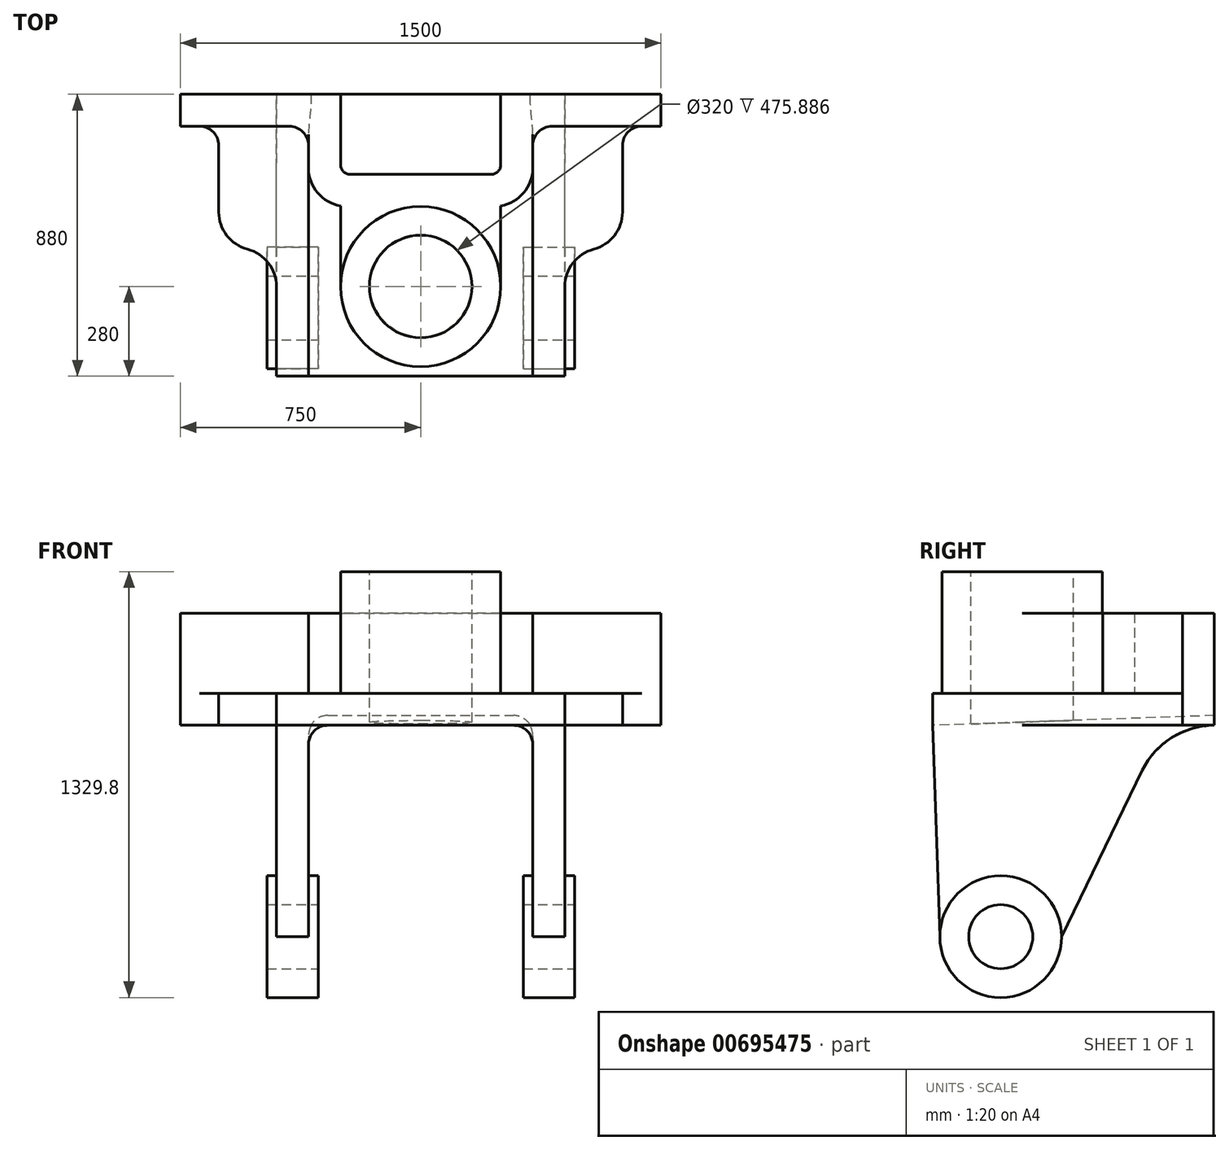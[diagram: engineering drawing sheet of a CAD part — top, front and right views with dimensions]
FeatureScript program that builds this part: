
annotation { "Feature Type Name" : "Feature", "Feature Type Description" : "" }
export const myFeature = defineFeature(function(context is Context, id is Id, definition is map)
    precondition{}
    {
        {
            var Q0;
            Q0=qCreatedBy(makeId("Top.planeOp"),FACE);
            var sketch = newSketch(context, id + "F0", { "sketchPlane" : qUnion([Q0])});
            skLineSegment(sketch, "E0.bottom", {"start": v(-750, 440) * mm, "end": v(750, 440) * mm});
            skLineSegment(sketch, "E0.top", {"start": v(-450, -440) * mm, "end": v(450, -440) * mm});
            skLineSegment(sketch, "E0.right", {"start": v(750, 440) * mm, "end": v(750, 340) * mm});
            skPoint(sketch, "E0.middle", {"position": v(0, 0) * mm});
            skArc(sketch, "E1", {"start": v(690, 340) * mm, "mid": v(647.57, 322.43) * mm, "end": v(630, 280) * mm});
            skLineSegment(sketch, "E2", {"start": v(450, -440) * mm, "end": v(450, -160) * mm});
            skArc(sketch, "E3", {"start": v(540, -43.81) * mm, "mid": v(475.13, -86.52) * mm, "end": v(450, -160) * mm});
            skArc(sketch, "E4.trimOffspring", {"start": v(540, -43.81) * mm, "mid": v(604.87, -1.1) * mm, "end": v(630, 72.38) * mm});
            skLineSegment(sketch, "E5.trimOffspring", {"start": v(690, 340) * mm, "end": v(750, 340) * mm});
            skLineSegment(sketch, "E6.trimOffspring", {"start": v(630, 280) * mm, "end": v(630, 72.38) * mm});
            skPoint(sketch, "E7.orphan", {"position": v(750, -440) * mm});
            skArc(sketch, "E8.MirrorCS", {"start": v(-540, -43.81) * mm, "mid": v(-475.13, -86.52) * mm, "end": v(-450, -160) * mm});
            skLineSegment(sketch, "E9.MirrorCS", {"start": v(-630, 280) * mm, "end": v(-630, 72.38) * mm});
            skArc(sketch, "E10.MirrorCS", {"start": v(-540, -43.81) * mm, "mid": v(-604.87, -1.1) * mm, "end": v(-630, 72.38) * mm});
            skPoint(sketch, "E11.MirrorP", {"position": v(-750, -440) * mm});
            skLineSegment(sketch, "E12.MirrorCS", {"start": v(-690, 340) * mm, "end": v(-750, 340) * mm});
            skLineSegment(sketch, "E13.MirrorCS", {"start": v(-750, 440) * mm, "end": v(-750, 340) * mm});
            skLineSegment(sketch, "E14.MirrorCS", {"start": v(-450, -440) * mm, "end": v(-450, -160) * mm});
            skArc(sketch, "E15.MirrorCS", {"start": v(-690, 340) * mm, "mid": v(-647.57, 322.43) * mm, "end": v(-630, 280) * mm});
            skSolve(sketch);
        }
        {
            var Q0;
            Q0=makeQuery(id+"F0.imprint","IMPRINT",FACE,{"disambiguationData":[TD([[makeQuery(id+"F0.imprint","IMPRINT",EDGE,{"derivedFrom":sQuery(id+"F0.wireOp",EDGE,"E0.bottom")}),-1.0]])]});
            extrude(context, id + "F1", {"entities" : qUnion([Q0]), "oppositeDirection" : true, "depth" : 100 * mm, "offsetDistance" : 25 * mm});
        }
        {
            var Q0;
            Q0=makeQuery(id+"F1.opExtrude","SWEPT_FACE",FACE,{"disambiguationData":[OSD([sQuery(id+"F0.wireOp",EDGE,"E2")])]});
            cPlane(context, id + "F2", {"entities" : qUnion([Q0]), "cplaneType" : CPlaneType.OFFSET, "offset" : 0 * mm, "width" : 150 * mm, "height" : 150 * mm});
        }
        {
            var Q0;
            Q0=makeQuery(id+"F1.opExtrude","CAP_FACE",FACE,{"disambiguationData":[OSD([sQuery(id+"F0.wireOp",EDGE,"E0.bottom"),sQuery(id+"F0.wireOp",EDGE,"E0.top"),sQuery(id+"F0.wireOp",EDGE,"E0.right"),sQuery(id+"F0.wireOp",EDGE,"E1"),sQuery(id+"F0.wireOp",EDGE,"E2"),sQuery(id+"F0.wireOp",EDGE,"E3"),sQuery(id+"F0.wireOp",EDGE,"E4.trimOffspring"),sQuery(id+"F0.wireOp",EDGE,"E5.trimOffspring"),sQuery(id+"F0.wireOp",EDGE,"E6.trimOffspring"),sQuery(id+"F0.wireOp",EDGE,"E8.MirrorCS"),sQuery(id+"F0.wireOp",EDGE,"E9.MirrorCS"),sQuery(id+"F0.wireOp",EDGE,"E10.MirrorCS"),sQuery(id+"F0.wireOp",EDGE,"E12.MirrorCS"),sQuery(id+"F0.wireOp",EDGE,"E13.MirrorCS"),sQuery(id+"F0.wireOp",EDGE,"E14.MirrorCS"),sQuery(id+"F0.wireOp",EDGE,"E15.MirrorCS")])],"isStart":true});
            var sketch = newSketch(context, id + "F3", { "sketchPlane" : qUnion([Q0])});
            skLineSegment(sketch, "E16", {"start": v(-250, 440) * mm, "end": v(-250, 220) * mm});
            skArc(sketch, "E17", {"start": v(-250, 220) * mm, "mid": v(-241.21, 198.79) * mm, "end": v(-220, 190) * mm});
            skLineSegment(sketch, "E18.trimOffspring", {"start": v(-220, 190) * mm, "end": v(220, 190) * mm});
            skLineSegment(sketch, "E19", {"start": v(250, 440) * mm, "end": v(250, 220) * mm});
            skArc(sketch, "E20", {"start": v(220, 190) * mm, "mid": v(241.21, 198.79) * mm, "end": v(250, 220) * mm});
            skLineSegment(sketch, "E21", {"start": v(-250, 440) * mm, "end": v(250, 440) * mm});
            skSolve(sketch);
        }
        {
            var Q0;
            {var subQ6=sQuery(id+"F3.wireOp",EDGE,"E16");Q0=makeQuery(id+"F3.imprint","IMPRINT",FACE,{"disambiguationData":[TD([[makeQuery(id+"F3.imprint","IMPRINT",EDGE,{"derivedFrom":subQ6}),-1.0]])]});}
            var sketch = newSketch(context, id + "F4", { "sketchPlane" : qUnion([Q0])});
            skLineSegment(sketch, "E22", {"start": v(750, 340) * mm, "end": v(410, 340) * mm});
            skLineSegment(sketch, "E23", {"start": v(350, 280) * mm, "end": v(350, 210) * mm});
            skLineSegment(sketch, "E24.trimOffspring", {"start": v(0, 190) * mm, "end": v(220, 190) * mm});
            skLineSegment(sketch, "E25", {"start": v(250, 440) * mm, "end": v(250, 220) * mm});
            skArc(sketch, "E26", {"start": v(220, 190) * mm, "mid": v(241.21, 198.79) * mm, "end": v(250, 220) * mm});
            skLineSegment(sketch, "E27.trimOffspring", {"start": v(250, 91.68) * mm, "end": v(250, -160) * mm});
            skArc(sketch, "E28", {"start": v(410, 340) * mm, "mid": v(367.57, 322.43) * mm, "end": v(350, 280) * mm});
            skArc(sketch, "E29", {"start": v(250, 91.68) * mm, "mid": v(321.65, 132.54) * mm, "end": v(350, 210) * mm});
            skLineSegment(sketch, "E30", {"start": v(750, 340) * mm, "end": v(750, 440) * mm});
            skLineSegment(sketch, "E31", {"start": v(750, 440) * mm, "end": v(250, 440) * mm});
            skArc(sketch, "E32.MirrorCS", {"start": v(-220, 190) * mm, "mid": v(-241.21, 198.79) * mm, "end": v(-250, 220) * mm});
            skLineSegment(sketch, "E33.MirrorCS", {"start": v(-750, 340) * mm, "end": v(-750, 440) * mm});
            skLineSegment(sketch, "E34.MirrorCS", {"start": v(-350, 280) * mm, "end": v(-350, 210) * mm});
            skArc(sketch, "E35.MirrorCS", {"start": v(-410, 340) * mm, "mid": v(-367.57, 322.43) * mm, "end": v(-350, 280) * mm});
            skArc(sketch, "E36.MirrorCS", {"start": v(-250, 91.68) * mm, "mid": v(-321.65, 132.54) * mm, "end": v(-350, 210) * mm});
            skLineSegment(sketch, "E37.MirrorCS", {"start": v(-750, 340) * mm, "end": v(-410, 340) * mm});
            skLineSegment(sketch, "E38.MirrorCS", {"start": v(0, 190) * mm, "end": v(-220, 190) * mm});
            skLineSegment(sketch, "E39.MirrorCS", {"start": v(-750, 440) * mm, "end": v(-250, 440) * mm});
            skLineSegment(sketch, "E40.MirrorCS", {"start": v(-250, 440) * mm, "end": v(-250, 220) * mm});
            skLineSegment(sketch, "E41.MirrorCS", {"start": v(-250, 91.68) * mm, "end": v(-250, -160) * mm});
            skArc(sketch, "E42", {"start": v(-250, -160) * mm, "mid": v(0, -410) * mm, "end": v(250, -160) * mm});
            skSolve(sketch);
        }
        {
            var Q0;
            Q0 = qSketchRegion(id + "F4", true);
            extrude(context, id + "F5", {"entities" : qUnion([Q0]), "operationType" : NewBodyOperationType.ADD, "depth" : 250 * mm, "offsetDistance" : 25 * mm});
        }
        {
            var Q0;
            Q0=makeQuery(id+"F5.opExtrude","CAP_FACE",FACE,{"disambiguationData":[OSD([sQuery(id+"F4.wireOp",EDGE,"E22"),sQuery(id+"F4.wireOp",EDGE,"E23"),sQuery(id+"F4.wireOp",EDGE,"E24.trimOffspring"),sQuery(id+"F4.wireOp",EDGE,"E25"),sQuery(id+"F4.wireOp",EDGE,"E26"),sQuery(id+"F4.wireOp",EDGE,"E27.trimOffspring"),sQuery(id+"F4.wireOp",EDGE,"E28"),sQuery(id+"F4.wireOp",EDGE,"E29"),sQuery(id+"F4.wireOp",EDGE,"E30"),sQuery(id+"F4.wireOp",EDGE,"E31"),sQuery(id+"F4.wireOp",EDGE,"E32.MirrorCS"),sQuery(id+"F4.wireOp",EDGE,"E33.MirrorCS"),sQuery(id+"F4.wireOp",EDGE,"E34.MirrorCS"),sQuery(id+"F4.wireOp",EDGE,"E35.MirrorCS"),sQuery(id+"F4.wireOp",EDGE,"E36.MirrorCS"),sQuery(id+"F4.wireOp",EDGE,"E37.MirrorCS"),sQuery(id+"F4.wireOp",EDGE,"E38.MirrorCS"),sQuery(id+"F4.wireOp",EDGE,"E39.MirrorCS"),sQuery(id+"F4.wireOp",EDGE,"E40.MirrorCS"),sQuery(id+"F4.wireOp",EDGE,"E41.MirrorCS"),sQuery(id+"F4.wireOp",EDGE,"E42")])],"isStart":false});
            var sketch = newSketch(context, id + "F6", { "sketchPlane" : qUnion([Q0])});
            skCircle(sketch, "E43", {"center": v(0, -160) * mm, "radius": 250 * mm});
            skSolve(sketch);
        }
        {
            var Q0;
            {var subQ0=sQuery(id+"F6.wireOp",EDGE,"E43");var subQ1=makeQuery(id+"F6.imprint","INTERSECT",VERTEX,{"derivedFrom":[makeQuery(id+"F5.opExtrude","CAP_EDGE",EDGE,{"disambiguationData":[OSD([sQuery(id+"F4.wireOp",EDGE,"E27.trimOffspring")])],"isStart":false}),subQ0]});Q0=makeQuery(id+"F6.imprint","IMPRINT",FACE,{"disambiguationData":[TD([[makeQuery(id+"F6.imprint","IMPRINT",EDGE,{"disambiguationData":[TD([[subQ1,-1.0]])],"derivedFrom":subQ0}),1.0]])]});}
            extrude(context, id + "F7", {"entities" : qUnion([Q0]), "operationType" : NewBodyOperationType.ADD, "depth" : 130 * mm, "offsetDistance" : 25 * mm});
        }
        {
            var Q0;
            Q0=makeQuery(id+"F7.opExtrude","CAP_FACE",FACE,{"disambiguationData":[OSD([sQuery(id+"F6.wireOp",EDGE,"E43")])],"isStart":false});
            var sketch = newSketch(context, id + "F8", { "sketchPlane" : qUnion([Q0])});
            skCircle(sketch, "E44", {"center": v(0, -160) * mm, "radius": 160 * mm});
            skSolve(sketch);
        }
        {
            var Q0;
            Q0=makeQuery(id+"F8.imprint","IMPRINT",FACE,{"disambiguationData":[TD([[makeQuery(id+"F8.imprint","IMPRINT",EDGE,{"derivedFrom":sQuery(id+"F8.wireOp",EDGE,"E44")}),1.0]])]});
            extrude(context, id + "F9", {"entities" : qUnion([Q0]), "operationType" : NewBodyOperationType.REMOVE, "endBound" : BoundingType.THROUGH_ALL, "oppositeDirection" : true, "depth" : 25 * mm, "offsetDistance" : 25 * mm});
        }
        {
            var Q0;
            Q0=qCreatedBy(id+"F2.planeOp",FACE);
            var sketch = newSketch(context, id + "F10", { "sketchPlane" : qUnion([Q0])});
            skPoint(sketch, "E45.0", {"position": v(440, -100) * mm});
            skPoint(sketch, "E46.0", {"position": v(-440, -100) * mm});
            skLineSegment(sketch, "E47", {"start": v(-440, -100) * mm, "end": v(440, -100) * mm});
            skLineSegment(sketch, "E48", {"start": v(440, -100) * mm, "end": v(440, -600) * mm, "construction": true});
            skArc(sketch, "E49", {"start": v(440, -100) * mm, "mid": v(307.33, -138.1) * mm, "end": v(215.1, -240.81) * mm});
            skLineSegment(sketch, "E50", {"start": v(-440, -100) * mm, "end": v(-416.97, -759.6) * mm});
            skLineSegment(sketch, "E51", {"start": v(-416.97, -759.6) * mm, "end": v(440, -760.5) * mm});
            skPoint(sketch, "E52", {"position": v(-36.97, -760) * mm});
            skLineSegment(sketch, "E53", {"start": v(-36.97, -760) * mm, "end": v(215.1, -240.81) * mm});
            skSolve(sketch);
        }
        {
            var Q0;
            Q0=makeQuery(id+"F10.imprint","IMPRINT",FACE,{"disambiguationData":[TD([[makeQuery(id+"F10.imprint","IMPRINT",EDGE,{"derivedFrom":sQuery(id+"F10.wireOp",EDGE,"E47")}),-1.0]])]});
            extrude(context, id + "F11", {"entities" : qUnion([Q0]), "operationType" : NewBodyOperationType.ADD, "oppositeDirection" : true, "depth" : 900 * mm, "offsetDistance" : 25 * mm});
        }
        {
            var Q0;
            Q0=makeQuery(id+"F11.opExtrude","SWEPT_FACE",FACE,{"disambiguationData":[OSD([sQuery(id+"F10.wireOp",EDGE,"E50")])]});
            var sketch = newSketch(context, id + "F12", { "sketchPlane" : qUnion([Q0])});
            skLineSegment(sketch, "E54", {"start": v(-350, -864.58) * mm, "end": v(-350, -144.58) * mm});
            skLineSegment(sketch, "E55", {"start": v(-290, -84.58) * mm, "end": v(290, -84.58) * mm});
            skArc(sketch, "E56", {"start": v(-290, -84.58) * mm, "mid": v(-332.43, -102.16) * mm, "end": v(-350, -144.58) * mm});
            skArc(sketch, "E57", {"start": v(350, -144.58) * mm, "mid": v(332.43, -102.16) * mm, "end": v(290, -84.58) * mm});
            skLineSegment(sketch, "E58", {"start": v(350, -144.58) * mm, "end": v(350, -864.58) * mm});
            skLineSegment(sketch, "E59", {"start": v(-350, -864.58) * mm, "end": v(350, -864.58) * mm});
            skSolve(sketch);
        }
        {
            var Q0;
            Q0 = qSketchRegion(id + "F12", true);
            extrude(context, id + "F13", {"entities" : qUnion([Q0]), "operationType" : NewBodyOperationType.REMOVE, "endBound" : BoundingType.THROUGH_ALL, "oppositeDirection" : true, "depth" : 25 * mm, "offsetDistance" : 25 * mm});
        }
        {
            var Q0;
            Q0=makeQuery(id+"F11.boolean.opBoolean","MERGE",FACE,{"derivedFrom":[makeQuery(id+"F1.opExtrude","SWEPT_FACE",FACE,{"disambiguationData":[OSD([sQuery(id+"F0.wireOp",EDGE,"E2")])]}),makeQuery(id+"F11.opExtrude","CAP_FACE",FACE,{"disambiguationData":[OSD([sQuery(id+"F10.wireOp",EDGE,"E47"),sQuery(id+"F10.wireOp",EDGE,"E49"),sQuery(id+"F10.wireOp",EDGE,"E50"),sQuery(id+"F10.wireOp",EDGE,"E51"),sQuery(id+"F10.wireOp",EDGE,"E53")])],"isStart":true})]});
            cPlane(context, id + "F14", {"entities" : qUnion([Q0]), "cplaneType" : CPlaneType.OFFSET, "offset" : 30 * mm, "width" : 150 * mm, "height" : 150 * mm});
        }
        {
            var Q0;
            Q0=qCreatedBy(id+"F14.planeOp",FACE);
            var sketch = newSketch(context, id + "F15", { "sketchPlane" : qUnion([Q0])});
            skPoint(sketch, "E60.0", {"position": v(-226.97, -759.8) * mm});
            skCircle(sketch, "E61", {"center": v(-226.97, -759.8) * mm, "radius": 190 * mm});
            skCircle(sketch, "E62", {"center": v(-226.97, -759.8) * mm, "radius": 100 * mm});
            skSolve(sketch);
        }
        {
            var Q0;
            Q0 = qSketchRegion(id + "F15", true);
            extrude(context, id + "F16", {"entities" : qUnion([Q0]), "operationType" : NewBodyOperationType.ADD, "oppositeDirection" : true, "depth" : 160 * mm, "offsetDistance" : 25 * mm});
        }
        {
            var Q0;
            Q0=makeQuery(id+"F15.imprint","IMPRINT",FACE,{"disambiguationData":[TD([[makeQuery(id+"F15.imprint","IMPRINT",EDGE,{"derivedFrom":sQuery(id+"F15.wireOp",EDGE,"E62")}),1.0]])]});
            extrude(context, id + "F17", {"entities" : qUnion([Q0]), "operationType" : NewBodyOperationType.REMOVE, "endBound" : BoundingType.THROUGH_ALL, "oppositeDirection" : true, "depth" : 25 * mm, "offsetDistance" : 25 * mm});
        }
        {
            var Q0;
            Q0=makeQuery(id+"F11.boolean.opBoolean","MERGE",FACE,{"derivedFrom":[makeQuery(id+"F1.opExtrude","SWEPT_FACE",FACE,{"disambiguationData":[OSD([sQuery(id+"F0.wireOp",EDGE,"E14.MirrorCS")])]}),makeQuery(id+"F11.opExtrude","CAP_FACE",FACE,{"disambiguationData":[OSD([sQuery(id+"F10.wireOp",EDGE,"E47"),sQuery(id+"F10.wireOp",EDGE,"E49"),sQuery(id+"F10.wireOp",EDGE,"E50"),sQuery(id+"F10.wireOp",EDGE,"E51"),sQuery(id+"F10.wireOp",EDGE,"E53")])],"isStart":false})]});
            cPlane(context, id + "F18", {"entities" : qUnion([Q0]), "cplaneType" : CPlaneType.OFFSET, "offset" : 30 * mm, "width" : 150 * mm, "height" : 150 * mm});
        }
        {
            var Q0;
            Q0=qCreatedBy(id+"F18.planeOp",FACE);
            var sketch = newSketch(context, id + "F19", { "sketchPlane" : qUnion([Q0])});
            skPoint(sketch, "E63.0", {"position": v(226.97, -759.8) * mm});
            skCircle(sketch, "E64", {"center": v(226.97, -759.8) * mm, "radius": 190 * mm});
            skCircle(sketch, "E65", {"center": v(226.97, -759.8) * mm, "radius": 100 * mm});
            skSolve(sketch);
        }
        {
            var Q0;
            Q0=makeQuery(id+"F19.imprint","IMPRINT",FACE,{"disambiguationData":[TD([[makeQuery(id+"F19.imprint","IMPRINT",EDGE,{"derivedFrom":sQuery(id+"F19.wireOp",EDGE,"E64")}),1.0]])]});
            extrude(context, id + "F20", {"entities" : qUnion([Q0]), "operationType" : NewBodyOperationType.ADD, "oppositeDirection" : true, "depth" : 160 * mm, "offsetDistance" : 25 * mm});
        }
    });
